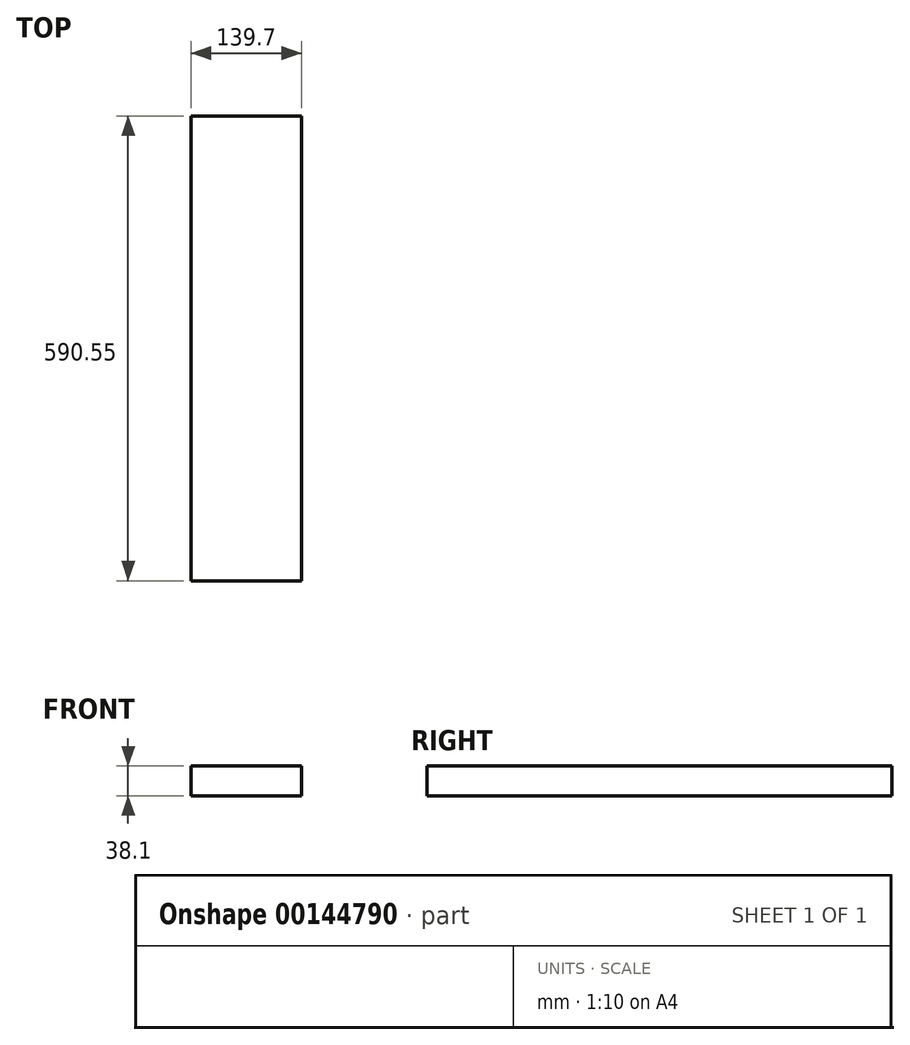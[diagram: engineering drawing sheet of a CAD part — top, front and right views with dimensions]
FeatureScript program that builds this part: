
annotation { "Feature Type Name" : "Feature", "Feature Type Description" : "" }
export const myFeature = defineFeature(function(context is Context, id is Id, definition is map)
    precondition{}
    {
        {
            var Q0;
            Q0=qCreatedBy(makeId("Front.planeOp"),FACE);
            var sketch = newSketch(context, id + "F0", { "sketchPlane" : qUnion([Q0])});
            skLineSegment(sketch, "E0.bottom", {"start": v(0, 0) * mm, "end": v(139.7, 0) * mm});
            skLineSegment(sketch, "E0.top", {"start": v(0, 38.1) * mm, "end": v(139.7, 38.1) * mm});
            skLineSegment(sketch, "E0.left", {"start": v(0, 0) * mm, "end": v(0, 38.1) * mm});
            skLineSegment(sketch, "E0.right", {"start": v(139.7, 0) * mm, "end": v(139.7, 38.1) * mm});
            skSolve(sketch);
        }
        {
            var Q0;
            Q0=makeQuery(id+"F0.imprint","IMPRINT",FACE,{"disambiguationData":[TD([[makeQuery(id+"F0.imprint","IMPRINT",EDGE,{"derivedFrom":sQuery(id+"F0.wireOp",EDGE,"E0.bottom")}),1.0]])]});
            extrude(context, id + "F1", {"entities" : qUnion([Q0]), "depth" : 590.55 * mm});
        }
    });
